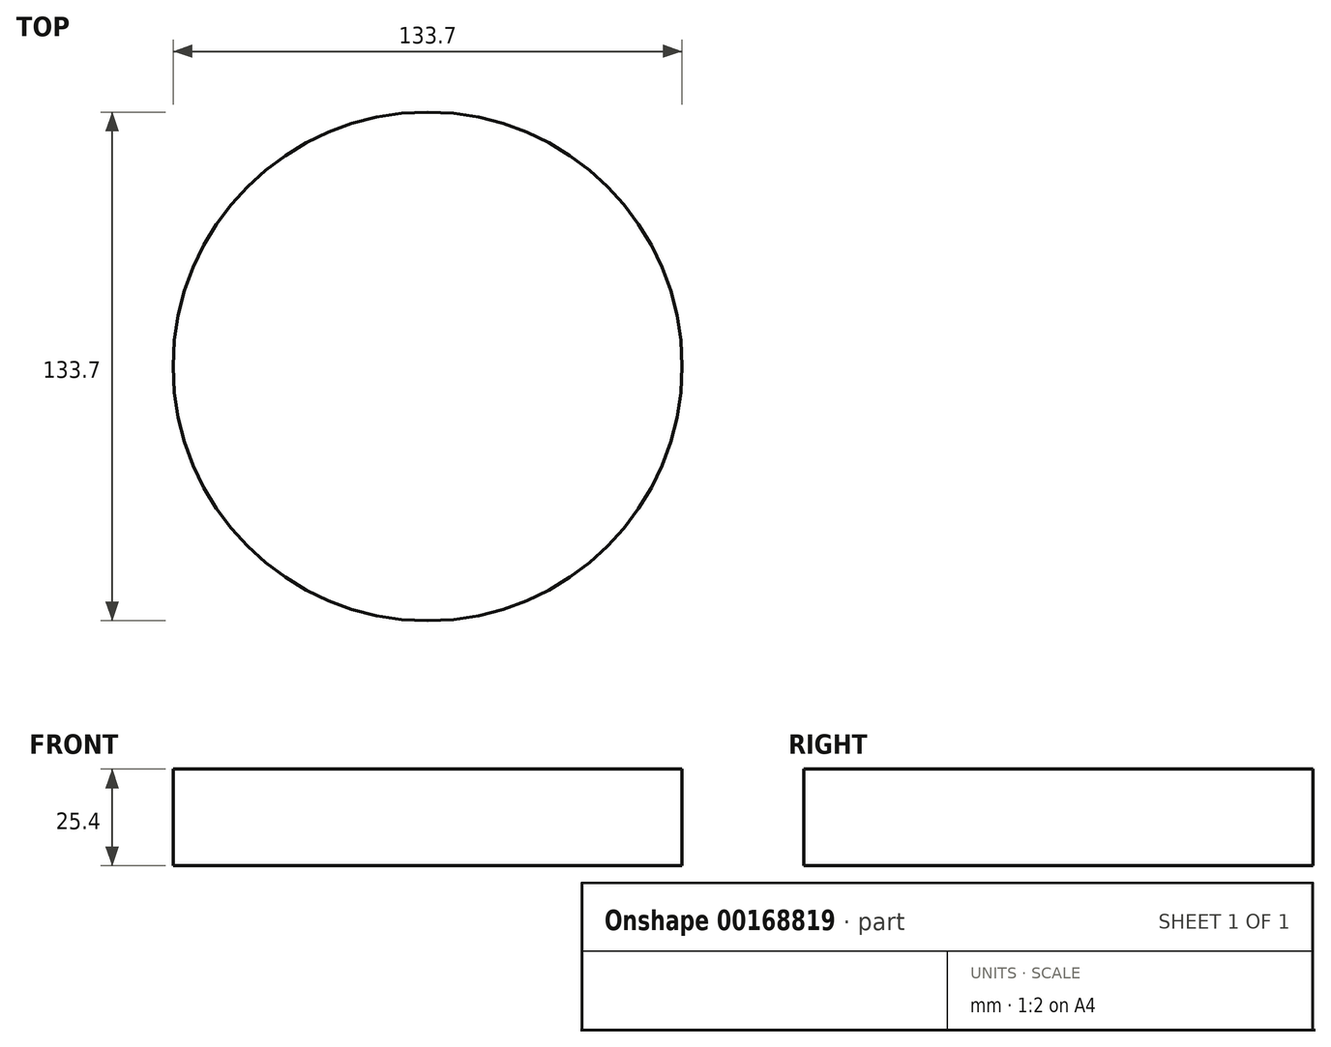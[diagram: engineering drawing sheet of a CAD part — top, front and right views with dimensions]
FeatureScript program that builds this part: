
annotation { "Feature Type Name" : "Feature", "Feature Type Description" : "" }
export const myFeature = defineFeature(function(context is Context, id is Id, definition is map)
    precondition{}
    {
        {
            var Q0;
            Q0=qCreatedBy(makeId("Top.planeOp"),FACE);
            var sketch = newSketch(context, id + "F0", { "sketchPlane" : qUnion([Q0])});
            skCircle(sketch, "E0", {"center": v(0, 0) * mm, "radius": 66.85 * mm});
            skSolve(sketch);
        }
        {
            var Q0;
            Q0 = qSketchRegion(id + "F0", true);
            extrude(context, id + "F4", {"entities" : qUnion([Q0]), "depth" : 25.4 * mm});
        }
    });
